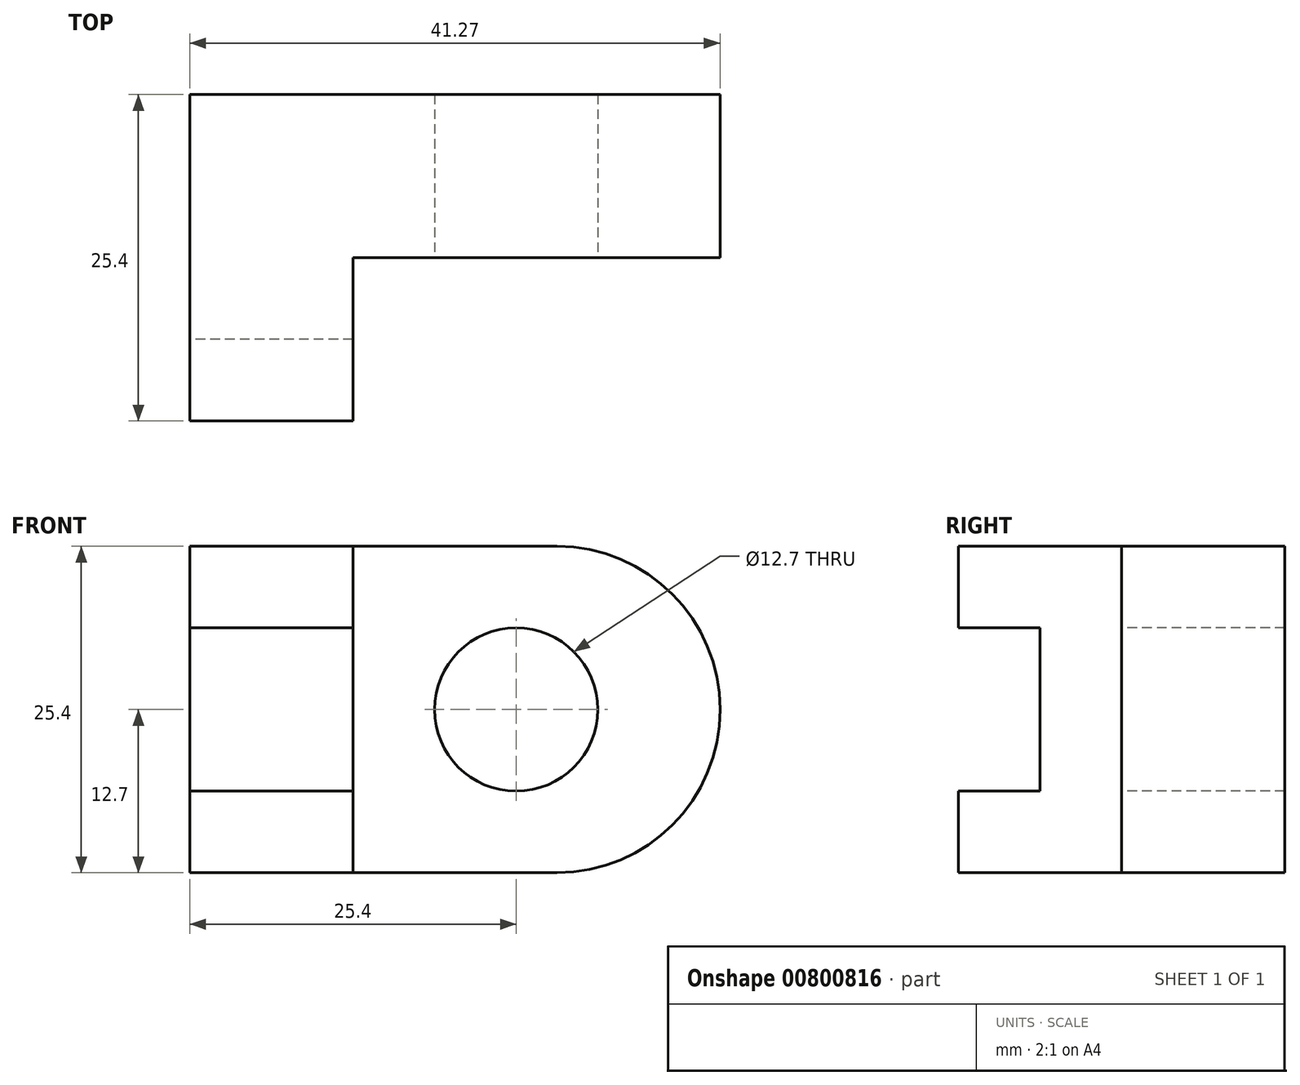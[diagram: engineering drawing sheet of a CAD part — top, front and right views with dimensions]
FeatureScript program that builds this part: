
annotation { "Feature Type Name" : "Feature", "Feature Type Description" : "" }
export const myFeature = defineFeature(function(context is Context, id is Id, definition is map)
    precondition{}
    {
        {
            var Q0;
            Q0=qCreatedBy(makeId("Front.planeOp"),FACE);
            var sketch = newSketch(context, id + "F0", { "sketchPlane" : qUnion([Q0])});
            skLineSegment(sketch, "E0", {"start": v(0, 0) * mm, "end": v(0, 25.4) * mm});
            skLineSegment(sketch, "E1", {"start": v(0, 25.4) * mm, "end": v(44.45, 25.4) * mm});
            skLineSegment(sketch, "E2", {"start": v(44.45, 25.4) * mm, "end": v(44.45, 0) * mm});
            skLineSegment(sketch, "E3", {"start": v(44.45, 0) * mm, "end": v(0, 0) * mm});
            skSolve(sketch);
        }
        {
            var Q0;
            Q0 = qSketchRegion(id + "F0", true);
            extrude(context, id + "F1", {"entities" : qUnion([Q0]), "depth" : 25.4 * mm, "offsetDistance" : 25.4 * mm});
        }
        {
            var Q0;
            Q0=makeQuery(id+"F1.opExtrude","SWEPT_FACE",FACE,{"disambiguationData":[OSD([sQuery(id+"F0.wireOp",EDGE,"E1")])]});
            var sketch = newSketch(context, id + "F2", { "sketchPlane" : qUnion([Q0])});
            skLineSegment(sketch, "E4", {"start": v(0, 0) * mm, "end": v(0, -25.4) * mm, "construction": true});
            skLineSegment(sketch, "E5", {"start": v(0, -25.4) * mm, "end": v(12.7, -25.4) * mm, "construction": true});
            skLineSegment(sketch, "E6", {"start": v(0, -25.4) * mm, "end": v(12.7, -25.4) * mm});
            skLineSegment(sketch, "E7", {"start": v(12.7, -12.7) * mm, "end": v(12.7, -25.4) * mm});
            skLineSegment(sketch, "E8", {"start": v(12.7, -12.7) * mm, "end": v(44.45, -12.7) * mm});
            skLineSegment(sketch, "E9", {"start": v(44.45, -12.7) * mm, "end": v(44.45, 0) * mm});
            skLineSegment(sketch, "E10", {"start": v(44.45, 0) * mm, "end": v(0, 0) * mm});
            skSolve(sketch);
        }
        {
            var Q0;
            {var subQ0=sQuery(id+"F2.wireOp",EDGE,"E7");Q0=makeQuery(id+"F2.imprint","IMPRINT",FACE,{"disambiguationData":[TD([[makeQuery(id+"F2.imprint","IMPRINT",EDGE,{"derivedFrom":subQ0}),1.0]])]});}
            extrude(context, id + "F3", {"entities" : qUnion([Q0]), "operationType" : NewBodyOperationType.REMOVE, "oppositeDirection" : true, "depth" : 25.4 * mm, "offsetDistance" : 25.4 * mm});
        }
        {
            var Q0;
            Q0=makeQuery(id+"F3.boolean.opBoolean","COPY",FACE,{"derivedFrom":makeQuery(id+"F3.opExtrude","SWEPT_FACE",FACE,{"disambiguationData":[OSD([sQuery(id+"F2.wireOp",EDGE,"E8")])]})});
            var sketch = newSketch(context, id + "F4", { "sketchPlane" : qUnion([Q0])});
            skLineSegment(sketch, "E11", {"start": v(28.58, 25.4) * mm, "end": v(28.58, 0) * mm, "construction": true});
            skLineSegment(sketch, "E12", {"start": v(28.58, 0) * mm, "end": v(12.7, 0) * mm, "construction": true});
            skLineSegment(sketch, "E13", {"start": v(12.7, 0) * mm, "end": v(12.7, 25.4) * mm, "construction": true});
            skArc(sketch, "E14", {"start": v(28.58, 0) * mm, "mid": v(41.28, 12.7) * mm, "end": v(28.58, 25.4) * mm});
            skSolve(sketch);
        }
        {
            var Q0;
            {var subQ0=sQuery(id+"F4.wireOp",EDGE,"E14");Q0=makeQuery(id+"F4.imprint","IMPRINT",FACE,{"disambiguationData":[TD([[makeQuery(id+"F4.imprint","IMPRINT",EDGE,{"derivedFrom":subQ0}),-1.0]])]});}
            extrude(context, id + "F5", {"entities" : qUnion([Q0]), "operationType" : NewBodyOperationType.REMOVE, "oppositeDirection" : true, "depth" : 25.4 * mm, "offsetDistance" : 25.4 * mm});
        }
        {
            var Q0;
            Q0=makeQuery(id+"F1.opExtrude","CAP_FACE",FACE,{"disambiguationData":[OSD([sQuery(id+"F0.wireOp",EDGE,"E0"),sQuery(id+"F0.wireOp",EDGE,"E1"),sQuery(id+"F0.wireOp",EDGE,"E2"),sQuery(id+"F0.wireOp",EDGE,"E3")])],"isStart":false});
            var sketch = newSketch(context, id + "F6", { "sketchPlane" : qUnion([Q0])});
            skLineSegment(sketch, "E15", {"start": v(12.7, 25.4) * mm, "end": v(12.7, 19.05) * mm, "construction": true});
            skLineSegment(sketch, "E16", {"start": v(12.7, 19.05) * mm, "end": v(0, 19.05) * mm});
            skLineSegment(sketch, "E17", {"start": v(0, 19.05) * mm, "end": v(0, 25.4) * mm});
            skLineSegment(sketch, "E18", {"start": v(0, 25.4) * mm, "end": v(12.7, 25.4) * mm});
            skLineSegment(sketch, "E19", {"start": v(12.7, 19.05) * mm, "end": v(12.7, 6.35) * mm});
            skLineSegment(sketch, "E20", {"start": v(12.7, 6.35) * mm, "end": v(0, 6.35) * mm});
            skLineSegment(sketch, "E21", {"start": v(0, 6.35) * mm, "end": v(0, 19.05) * mm});
            skLineSegment(sketch, "E22", {"start": v(0, 6.35) * mm, "end": v(0, 0) * mm});
            skLineSegment(sketch, "E23", {"start": v(0, 0) * mm, "end": v(12.7, 0) * mm});
            skSolve(sketch);
        }
        {
            var Q0;
            Q0=makeQuery(id+"F6.imprint","IMPRINT",FACE,{"disambiguationData":[TD([[makeQuery(id+"F6.imprint","IMPRINT",EDGE,{"derivedFrom":sQuery(id+"F6.wireOp",EDGE,"E16")}),1.0]])]});
            extrude(context, id + "F7", {"entities" : qUnion([Q0]), "operationType" : NewBodyOperationType.REMOVE, "oppositeDirection" : true, "depth" : 6.35 * mm, "offsetDistance" : 25.4 * mm});
        }
        {
            var Q0;
            Q0=makeQuery(id+"F3.boolean.opBoolean","COPY",FACE,{"derivedFrom":makeQuery(id+"F3.opExtrude","SWEPT_FACE",FACE,{"disambiguationData":[OSD([sQuery(id+"F2.wireOp",EDGE,"E8")])]})});
            var sketch = newSketch(context, id + "F8", { "sketchPlane" : qUnion([Q0])});
            skLineSegment(sketch, "E24", {"start": v(12.7, 25.4) * mm, "end": v(12.7, 19.05) * mm, "construction": true});
            skLineSegment(sketch, "E25", {"start": v(12.7, 19.05) * mm, "end": v(12.7, 6.35) * mm, "construction": true});
            skLineSegment(sketch, "E26", {"start": v(12.7, 6.35) * mm, "end": v(12.7, 0) * mm, "construction": true});
            skLineSegment(sketch, "E27", {"start": v(12.7, 0) * mm, "end": v(12.7, 6.35) * mm, "construction": true});
            skLineSegment(sketch, "E28", {"start": v(15.58, 6.35) * mm, "end": v(28.28, 6.35) * mm, "construction": true});
            skLineSegment(sketch, "E29", {"start": v(28.28, 6.35) * mm, "end": v(28.28, 19.05) * mm, "construction": true});
            skLineSegment(sketch, "E30", {"start": v(28.28, 19.05) * mm, "end": v(12.7, 19.05) * mm, "construction": true});
            skLineSegment(sketch, "E31", {"start": v(12.7, 6.35) * mm, "end": v(19.05, 6.35) * mm, "construction": true});
            skLineSegment(sketch, "E32", {"start": v(19.05, 6.35) * mm, "end": v(19.05, 19.05) * mm, "construction": true});
            skLineSegment(sketch, "E33", {"start": v(12.7, 19.05) * mm, "end": v(19.05, 19.05) * mm, "construction": true});
            skLineSegment(sketch, "E34", {"start": v(19.05, 19.05) * mm, "end": v(31.75, 19.05) * mm, "construction": true});
            skLineSegment(sketch, "E35", {"start": v(31.75, 19.05) * mm, "end": v(31.75, 6.35) * mm, "construction": true});
            skLineSegment(sketch, "E36", {"start": v(12.7, 12.7) * mm, "end": v(25.4, 12.7) * mm, "construction": true});
            skPoint(sketch, "E36.endSnap0", {"position": v(19.05, 12.7) * mm});
            skCircle(sketch, "E37", {"center": v(25.4, 12.7) * mm, "radius": 6.35 * mm});
            skSolve(sketch);
        }
        {
            var Q0;
            Q0=makeQuery(id+"F8.imprint","IMPRINT",FACE,{"disambiguationData":[TD([[makeQuery(id+"F8.imprint","IMPRINT",EDGE,{"derivedFrom":sQuery(id+"F8.wireOp",EDGE,"E37")}),1.0]])]});
            extrude(context, id + "F9", {"entities" : qUnion([Q0]), "operationType" : NewBodyOperationType.REMOVE, "endBound" : BoundingType.UP_TO_NEXT, "oppositeDirection" : true, "depth" : 25.4 * mm, "offsetDistance" : 25.4 * mm});
        }
    });
